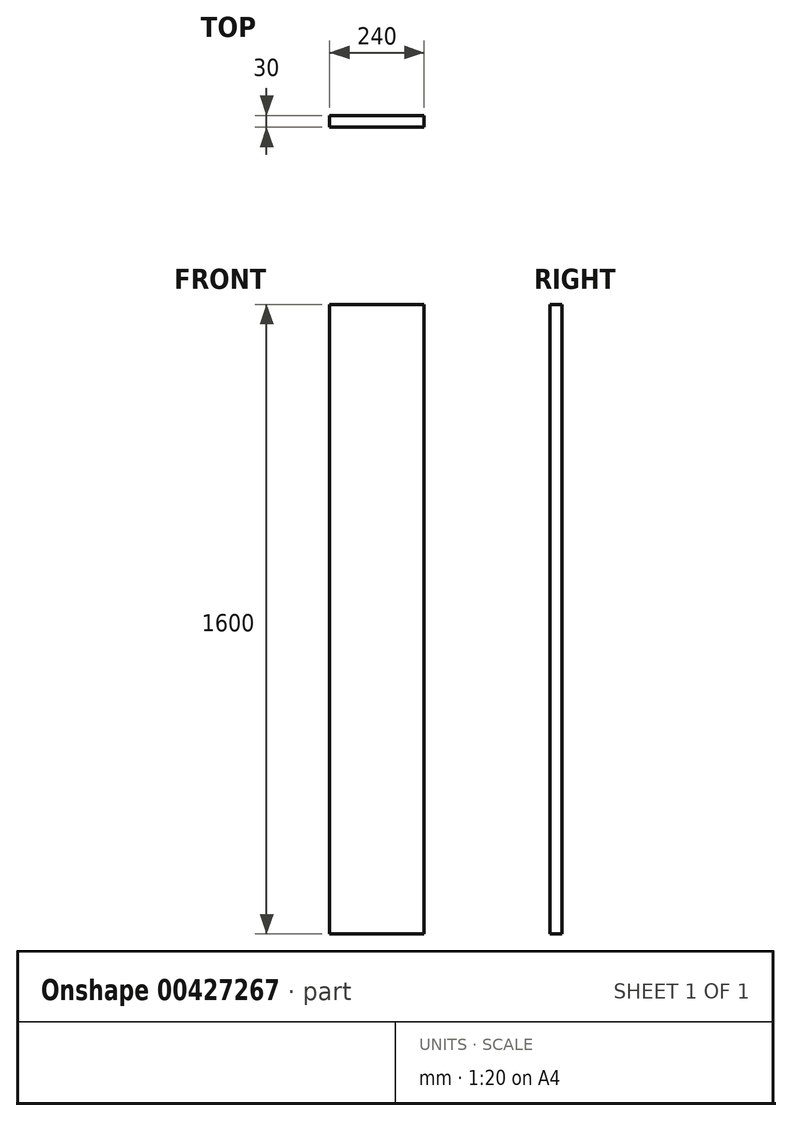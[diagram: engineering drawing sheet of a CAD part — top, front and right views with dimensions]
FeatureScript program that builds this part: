
annotation { "Feature Type Name" : "Feature", "Feature Type Description" : "" }
export const myFeature = defineFeature(function(context is Context, id is Id, definition is map)
    precondition{}
    {
        {
            var Q0;
            Q0=qCreatedBy(makeId("Front.planeOp"),FACE);
            var sketch = newSketch(context, id + "F0", { "sketchPlane" : qUnion([Q0])});
            skLineSegment(sketch, "E0.bottom", {"start": v(0, 0) * mm, "end": v(-240, 0) * mm});
            skLineSegment(sketch, "E0.top", {"start": v(0, 1600) * mm, "end": v(-240, 1600) * mm});
            skLineSegment(sketch, "E0.left", {"start": v(0, 0) * mm, "end": v(0, 1600) * mm});
            skLineSegment(sketch, "E0.right", {"start": v(-240, 0) * mm, "end": v(-240, 1600) * mm});
            skSolve(sketch);
        }
        {
            var Q0;
            Q0=makeQuery(id+"F0.imprint","IMPRINT",FACE,{"disambiguationData":[TD([[makeQuery(id+"F0.imprint","IMPRINT",EDGE,{"derivedFrom":sQuery(id+"F0.wireOp",EDGE,"E0.bottom")}),-1.0]])]});
            extrude(context, id + "F1", {"entities" : qUnion([Q0]), "depth" : 30 * mm, "offsetDistance" : 25 * mm});
        }
    });
